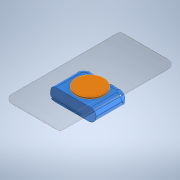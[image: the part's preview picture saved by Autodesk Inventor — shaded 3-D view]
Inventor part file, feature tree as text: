
AUTODESK INVENTOR PART (.ipt)
format: ipt  version: 2022 (Build 260153000, 153)  size: 1,069,568 bytes
history: native  units: mm
features: fillet x23, extrude x19, sketch x19, other x4, chamfer x2, plane x1, mirror x1
ambient origin geometry x8: Origin, YZ Plane, XZ Plane, XY Plane, X Axis, Y Axis, Z Axis, Center Point
bodies: Body1 (feature_tree), Body2 (feature_tree), Body3 (feature_tree), Body4 (feature_tree)
feature tree (69):
  other  "Popsocket"
  extrude  "Extrusion1"  Depth=1.26mm TaperAngle=0.0deg
  extrude  "Extrusion2"  Depth=3.5mm
  extrude  "Extrusion3"  Depth=4.26mm TaperAngle=0.0deg
  fillet  "Fillet1"  Radius=5.0mm
  extrude  "Extrusion4"  Depth=4.3mm TaperAngle=0.0deg
  extrude  "Extrusion5"  Depth=2.0mm TaperAngle=0.0deg
  fillet  "Fillet4"  Radius=150.0mm
  fillet  "Fillet5"  Radius=71.0mm
  chamfer  "Chamfer1"  Distance=10.0mm
  fillet  "Fillet6"  Radius=5.0mm
  extrude  "Extrusion6"  Depth=1.0mm
  fillet  "Fillet2"  Radius=1.0mm
  fillet  "Fillet3"  Radius=0.2mm
  extrude  "Extrusion7"  Depth=3.0mm TaperAngle=0.0deg
  extrude  "Extrusion8"  TaperAngle=0.0deg  [1 undecoded]
  plane  "Work Plane1"
  extrude  "Extrusion9"  TaperAngle=0.0deg  [1 undecoded]
  extrude  "Extrusion10"  Depth=8.0mm
  extrude  "Extrusion11"  Depth=1.5mm
  fillet  "Fillet7"  Radius=21.0mm
  fillet  "Fillet8"  Radius=21.0mm
  extrude  "Extrusion12"  Depth=40.0mm TaperAngle=0.0deg
  extrude  "Extrusion13"  Depth=18.0mm
  extrude  "Extrusion14"  Depth=40.0mm TaperAngle=0.0deg
  extrude  "Extrusion15"  Depth=3.0mm
  chamfer  "Chamfer2"  Distance=30.0mm
  fillet  "Fillet9"  Radius=22.0mm
  fillet  "Fillet10"  Radius=22.0mm
  fillet  "Fillet11"  Radius=3.0mm
  fillet  "Fillet12"  Radius=10.0mm
  fillet  "Fillet13"  Radius=10.0mm
  extrude  "Extrusion16"  Depth=0.1mm
  fillet  "Fillet14"  Radius=9.75mm
  mirror  "Mirror1"
  extrude  "Extrusion17"  Depth=9.75mm TaperAngle=0.0deg
  extrude  "Extrusion18"  Depth=12.0mm
  extrude  "Extrusion19"  Depth=9.75mm
  fillet  "Fillet16"  Radius=1.32mm
  fillet  "Fillet17"  Radius=1.26mm
  fillet  "Fillet18"  Radius=2.1mm
  fillet  "Fillet19"  Radius=6.0mm
  fillet  "Fillet20"  Radius=4.0mm
  fillet  "Fillet21"  Radius=1.7mm
  fillet  "Fillet22"  Radius=10.0mm
  fillet  "Fillet23"  Radius=1.0mm
  fillet  "Fillet24"  Radius=2.0mm
  sketch  "Sketch1"  dims[d0=39.99mm d1=1.26mm d2=0.0mm]
  sketch  "Sketch2"  dims[d3=35.5mm d4=3.5mm d5=0.349066mm]
  sketch  "Sketch3"  dims[d6=22.0mm d7=4.26mm d8=0.0mm d9=5.0mm]
  sketch  "Sketch4"  dims[d10=14.43mm d11=4.3mm d12=0.0mm]
  sketch  "Sketch5"  dims[d13=36.7mm d14=2.0mm d15=0.0mm d16=150.0mm d17=71.0mm]
  sketch  "Sketch6"  dims[d18=75.0mm]
  other  "Phone"
  sketch  "Sketch7"  dims[d19=35.5mm d20=10.0mm d21=0.0mm d22=5.0mm]
  other  "Holster"
  sketch  "Sketch8"  dims[d23=4.9mm d24=1.0mm d25=1.0mm]
  sketch  "Sketch9"  dims[d26=1.0mm d27=2.0mm d28=60.0deg d29=0.2mm]
  sketch  "Sketch10"  dims[d30=60.0mm d31=3.0mm d32=0.0mm]
  sketch  "Sketch12"  dims[d33=0.1mm d34=0.0mm]
  sketch  "Sketch13"  dims[d35=3.0mm d36=0.0mm d37=0.0mm]
  other  "HolsterV2"
  sketch  "Sketch14"  dims[d38=8.0mm d39=8.0mm]
  sketch  "Sketch15"  dims[d41=11.17mm d42=0.0mm d43=1.5mm d44=21.0mm d45=21.0mm]
  sketch  "Sketch16"  dims[d46=0.1mm d47=40.0mm d48=0.0mm]
  sketch  "Sketch17"  dims[d53=18.0mm d54=18.0mm]
  sketch  "Sketch18"  dims[d55=3.0mm d56=40.0mm d57=0.0mm]
  sketch  "Sketch19"  dims[d58=3.0mm d59=3.0mm]
  sketch  "Sketch21"  dims[d60=30.0mm d61=30.0mm d62=22.0mm d63=22.0mm d64=3.0mm d65=0.0mm d66=10.0mm d67=10.0mm d68=0.1mm d69=9.75mm d70=0.0mm d71=9.75mm d72=0.0mm d73=12.0mm d74=9.75mm d75=1.32mm d76=1.26mm d77=2.1mm d78=6.0mm d79=4.0mm d80=1.7mm d81=10.0mm d82=0.0mm d83=1.0mm d84=2.0mm d85=45.0deg d86=2.0mm d87=10.0mm d88=7.0mm d89=2.0mm d90=4.0mm d92=7.0mm d93=1.5mm d94=0.0mm d95=6.0mm d97=20.0mm d98=40.0mm d99=1.0mm d100=0.0mm d101=2.0mm d102=0.0mm d103=19.4mm d104=0.8mm d105=2.0mm d106=0.0mm d107=10.0mm d108=10.0mm d109=0.5mm d110=2.0mm d111=2.0mm d112=2.0mm d113=0.2mm d114=25.25mm d115=0.9mm d116=3.0mm]
note: 2 required parameter values undecoded (feature->parameter linkage not recoverable at this tier; creation-order binding heuristic only, values carry confidence <= 0.55)
